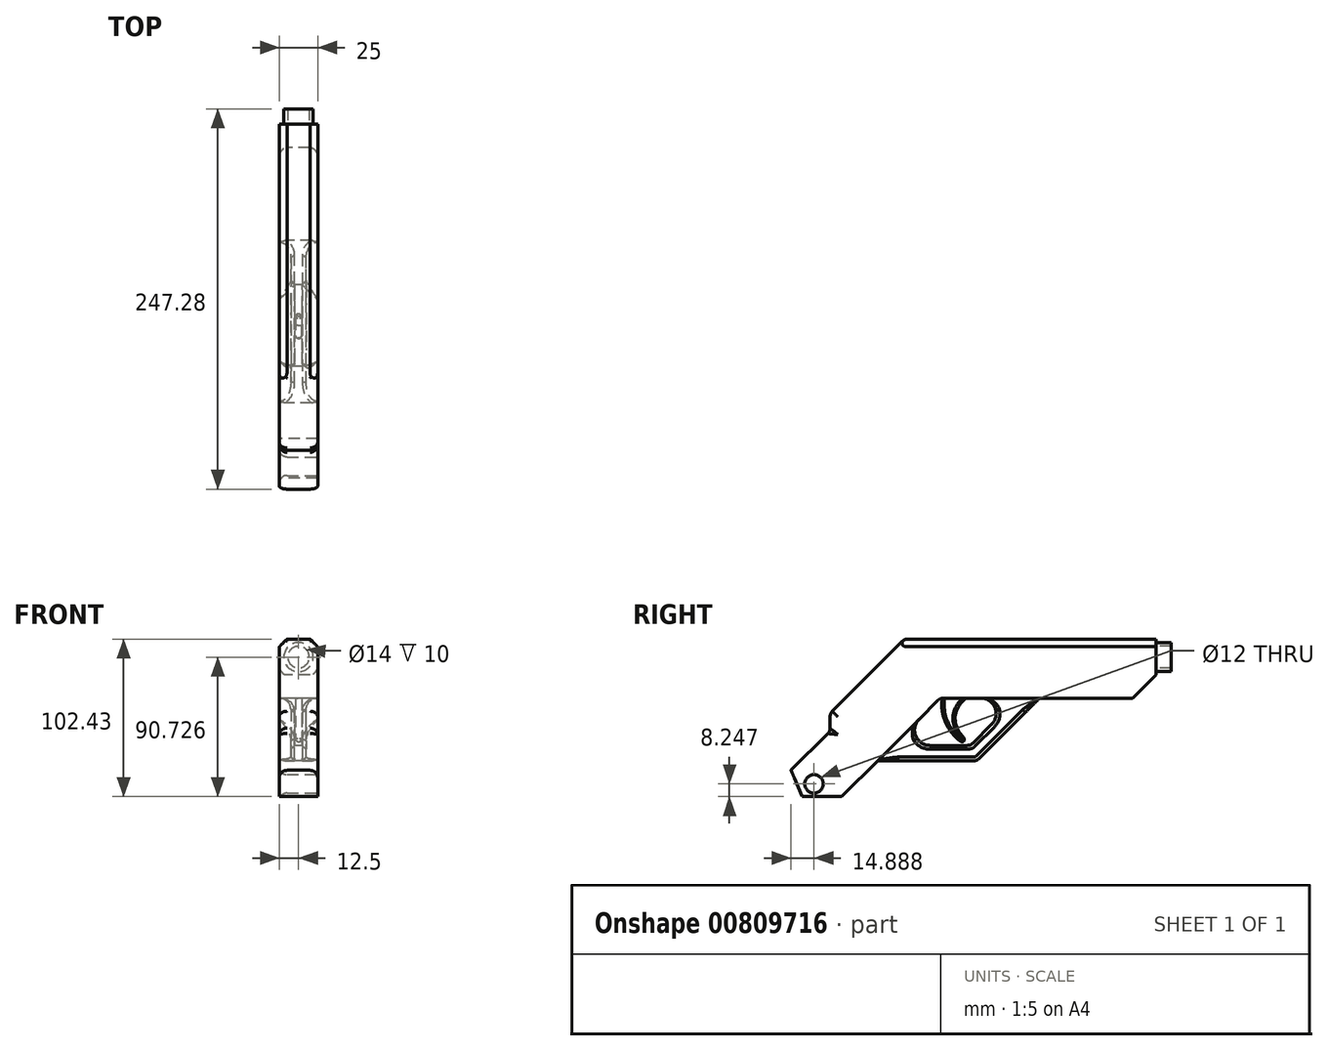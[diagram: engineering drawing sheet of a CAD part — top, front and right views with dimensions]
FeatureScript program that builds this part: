
annotation { "Feature Type Name" : "Feature", "Feature Type Description" : "" }
export const myFeature = defineFeature(function(context is Context, id is Id, definition is map)
    precondition{}
    {
        {
            var Q0;
            Q0=qCreatedBy(makeId("Right.planeOp"),FACE);
            var sketch = newSketch(context, id + "F0", { "sketchPlane" : qUnion([Q0])});
            skLineSegment(sketch, "E0", {"start": v(-96.29, 0) * mm, "end": v(-96.29, 15) * mm});
            skLineSegment(sketch, "E1", {"start": v(-96.29, 15) * mm, "end": v(75.64, 15) * mm});
            skLineSegment(sketch, "E2", {"start": v(75.64, 15) * mm, "end": v(75.64, 0) * mm});
            skLineSegment(sketch, "E3", {"start": v(75.64, 0) * mm, "end": v(60.55, -15) * mm});
            skLineSegment(sketch, "E4", {"start": v(60.55, -15) * mm, "end": v(0, -15) * mm});
            skLineSegment(sketch, "E5", {"start": v(0, -15) * mm, "end": v(-10, -25) * mm});
            skLineSegment(sketch, "E6", {"start": v(-10, -25) * mm, "end": v(-96.29, -25) * mm});
            skLineSegment(sketch, "E7", {"start": v(-96.29, -25) * mm, "end": v(-96.29, 0) * mm});
            skLineSegment(sketch, "E8", {"start": v(-96.29, 15) * mm, "end": v(-136.29, -25) * mm});
            skLineSegment(sketch, "E9", {"start": v(-136.29, -25) * mm, "end": v(-136.29, -36.6) * mm});
            skLineSegment(sketch, "E10", {"start": v(-136.29, -36.6) * mm, "end": v(-178.71, -79.02) * mm});
            skLineSegment(sketch, "E11", {"start": v(-178.71, -79.02) * mm, "end": v(-128.71, -79.02) * mm});
            skLineSegment(sketch, "E12", {"start": v(-128.71, -79.02) * mm, "end": v(-74.7, -25) * mm});
            skLineSegment(sketch, "E13", {"start": v(-10, -25) * mm, "end": v(-40.76, -55.76) * mm});
            skLineSegment(sketch, "E14", {"start": v(-40.76, -55.76) * mm, "end": v(-105.46, -55.76) * mm});
            skLineSegment(sketch, "E15", {"start": v(-24.14, -25) * mm, "end": v(-44.9, -45.76) * mm});
            skLineSegment(sketch, "E16", {"start": v(-44.9, -45.76) * mm, "end": v(-95.46, -45.76) * mm});
            skLineSegment(sketch, "E17", {"start": v(-96.29, 15) * mm, "end": v(-87.88, 23.41) * mm});
            skLineSegment(sketch, "E18", {"start": v(-87.88, 23.41) * mm, "end": v(75.64, 23.41) * mm});
            skLineSegment(sketch, "E19", {"start": v(75.64, 23.41) * mm, "end": v(75.64, 15) * mm});
            skLineSegment(sketch, "E20", {"start": v(-74.7, -25) * mm, "end": v(-64.7, -15) * mm});
            skLineSegment(sketch, "E21", {"start": v(-64.7, -15) * mm, "end": v(0, -15) * mm});
            skLineSegment(sketch, "E22", {"start": v(-24.14, -25) * mm, "end": v(-14.14, -15) * mm});
            skSolve(sketch);
        }
        {
            var Q0;
            Q0=makeQuery(id+"F0.imprint","IMPRINT",FACE,{"disambiguationData":[TD([[makeQuery(id+"F0.imprint","IMPRINT",EDGE,{"derivedFrom":sQuery(id+"F0.wireOp",EDGE,"E0")}),1.0]])]});
            var Q1;
            Q1=makeQuery(id+"F0.imprint","IMPRINT",FACE,{"disambiguationData":[TD([[makeQuery(id+"F0.imprint","IMPRINT",EDGE,{"derivedFrom":sQuery(id+"F0.wireOp",EDGE,"E0")}),-1.0]])]});
            var Q2;
            {var subQ1=sQuery(id+"F0.wireOp",EDGE,"E13");Q2=makeQuery(id+"F0.imprint","IMPRINT",FACE,{"disambiguationData":[TD([[makeQuery(id+"F0.imprint","IMPRINT",EDGE,{"derivedFrom":subQ1}),-1.0]])]});}
            var Q3;
            Q3=makeQuery(id+"F0.imprint","IMPRINT",FACE,{"disambiguationData":[TD([[makeQuery(id+"F0.imprint","IMPRINT",EDGE,{"derivedFrom":sQuery(id+"F0.wireOp",EDGE,"E1")}),1.0]])]});
            var Q4;
            {var subQ0=sQuery(id+"F0.wireOp",EDGE,"E5");Q4=makeQuery(id+"F0.imprint","IMPRINT",FACE,{"disambiguationData":[TD([[makeQuery(id+"F0.imprint","IMPRINT",EDGE,{"derivedFrom":subQ0}),-1.0]])]});}
            extrude(context, id + "F1", {"entities" : qUnion([Q0, Q1, Q2, Q3, Q4]), "depth" : 12.5 * mm});
        }
        {
            var Q0;
            Q0=makeQuery(id+"F1.opExtrude","CAP_EDGE",EDGE,{"disambiguationData":[OSD([sQuery(id+"F0.wireOp",EDGE,"E18")])],"isStart":false});
            chamfer(context, id + "F2", {"entities" : qUnion([Q0]), "width" : 5 * mm, "tangentPropagation" : true});
        }
        {
            var Q0;
            {var subQ0=makeQuery(id+"F1.opExtrude","SWEPT_EDGE",EDGE,{"disambiguationData":[OSD([sQuery(id+"F0.wireOp",EDGE,"E10"),sQuery(id+"F0.wireOp",EDGE,"E11")])]});Q0=makeQuery(id+"F9.boolean.opBoolean","MERGE",EDGE,{"derivedFrom":[subQ0,makeQuery(id+"F9.opPattern","COPY",EDGE,{"derivedFrom":subQ0,"instanceName":"1"})]});}
            chamfer(context, id + "F3", {"entities" : qUnion([Q0]), "width" : 10 * mm, "tangentPropagation" : true});
        }
        {
            var Q0;
            {var subQ0=makeQuery(id+"F1.opExtrude","SWEPT_EDGE",EDGE,{"disambiguationData":[OSD([sQuery(id+"F0.wireOp",EDGE,"E12"),sQuery(id+"F0.wireOp",EDGE,"E16")])]});Q0=makeQuery(id+"F9.boolean.opBoolean","MERGE",EDGE,{"derivedFrom":[subQ0,makeQuery(id+"F9.opPattern","COPY",EDGE,{"derivedFrom":subQ0,"instanceName":"1"})]});}
            var Q1;
            {var subQ0=makeQuery(id+"F1.opExtrude","SWEPT_EDGE",EDGE,{"disambiguationData":[OSD([sQuery(id+"F0.wireOp",EDGE,"E21"),sQuery(id+"F0.wireOp",EDGE,"E22")])]});Q1=makeQuery(id+"F9.boolean.opBoolean","MERGE",EDGE,{"derivedFrom":[subQ0,makeQuery(id+"F9.opPattern","COPY",EDGE,{"derivedFrom":subQ0,"instanceName":"1"})]});}
            fillet(context, id + "F4", {"entities" : qUnion([Q0, Q1]), "radius" : 10 * mm, "tangentPropagation" : true, "allowEdgeOverflow" : false});
        }
        {
            var Q0;
            Q0=makeQuery(id+"F1.opExtrude","CAP_FACE",FACE,{"disambiguationData":[OSD([sQuery(id+"F0.wireOp",EDGE,"E2"),sQuery(id+"F0.wireOp",EDGE,"E3"),sQuery(id+"F0.wireOp",EDGE,"E4"),sQuery(id+"F0.wireOp",EDGE,"E5"),sQuery(id+"F0.wireOp",EDGE,"E8"),sQuery(id+"F0.wireOp",EDGE,"E9"),sQuery(id+"F0.wireOp",EDGE,"E10"),sQuery(id+"F0.wireOp",EDGE,"E11"),sQuery(id+"F0.wireOp",EDGE,"E12"),sQuery(id+"F0.wireOp",EDGE,"E13"),sQuery(id+"F0.wireOp",EDGE,"E14"),sQuery(id+"F0.wireOp",EDGE,"E15"),sQuery(id+"F0.wireOp",EDGE,"E16"),sQuery(id+"F0.wireOp",EDGE,"E17"),sQuery(id+"F0.wireOp",EDGE,"E18"),sQuery(id+"F0.wireOp",EDGE,"E19"),sQuery(id+"F0.wireOp",EDGE,"E20"),sQuery(id+"F0.wireOp",EDGE,"E21"),sQuery(id+"F0.wireOp",EDGE,"E22")])],"isStart":false});
            var sketch = newSketch(context, id + "F5", { "sketchPlane" : qUnion([Q0])});
            skLineSegment(sketch, "E23.0", {"start": v(-128.71, -79.02) * mm, "end": v(-105.46, -55.76) * mm});
            skLineSegment(sketch, "E24.0", {"start": v(-40.76, -55.76) * mm, "end": v(-105.46, -55.76) * mm});
            skLineSegment(sketch, "E25.0", {"start": v(0, -15) * mm, "end": v(-40.76, -55.76) * mm});
            skLineSegment(sketch, "E26.0", {"start": v(-78.39, -28.7) * mm, "end": v(-64.7, -15) * mm});
            skLineSegment(sketch, "E27", {"start": v(-105.46, -55.76) * mm, "end": v(-78.39, -28.7) * mm});
            skLineSegment(sketch, "E28", {"start": v(-64.7, -15) * mm, "end": v(0, -15) * mm});
            skSolve(sketch);
        }
        {
            var Q0;
            Q0=makeQuery(id+"F5.imprint","IMPRINT",FACE,{"disambiguationData":[TD([[makeQuery(id+"F5.imprint","IMPRINT",EDGE,{"derivedFrom":sQuery(id+"F5.wireOp",EDGE,"E24.0")}),-1.0]])]});
            extrude(context, id + "F6", {"entities" : qUnion([Q0]), "operationType" : NewBodyOperationType.REMOVE, "oppositeDirection" : true, "depth" : 7.5 * mm});
        }
        {
            var Q0;
            {var subQ0=sQuery(id+"F0.wireOp",EDGE,"E12");Q0=makeQuery(id+"F6.boolean.opBoolean","MERGE",EDGE,{"derivedFrom":[makeQuery(id+"F1.opExtrude","CAP_EDGE",EDGE,{"disambiguationData":[OSD([subQ0])],"isStart":false}),makeQuery(id+"F1.opExtrude","CAP_EDGE",EDGE,{"disambiguationData":[OSD([subQ0,sQuery(id+"F0.wireOp",EDGE,"E20")])],"isStart":false}),makeQuery(id+"F6.opExtrude","CAP_EDGE",EDGE,{"disambiguationData":[OSD([sQuery(id+"F5.wireOp",EDGE,"E27")])],"isStart":true})]});}
            var Q1;
            Q1=makeQuery(id+"F1.opExtrude","CAP_EDGE",EDGE,{"disambiguationData":[OSD([sQuery(id+"F0.wireOp",EDGE,"E10")])],"isStart":false});
            var Q2;
            Q2=makeQuery(id+"F1.opExtrude","CAP_EDGE",EDGE,{"disambiguationData":[OSD([sQuery(id+"F0.wireOp",EDGE,"E9")])],"isStart":false});
            var Q3;
            Q3=makeQuery(id+"F1.opExtrude","CAP_EDGE",EDGE,{"disambiguationData":[OSD([sQuery(id+"F0.wireOp",EDGE,"E8"),sQuery(id+"F0.wireOp",EDGE,"E17")])],"isStart":false});
            fillet(context, id + "F7", {"entities" : qUnion([Q0, Q1, Q2, Q3]), "radius" : 5 * mm, "tangentPropagation" : true, "allowEdgeOverflow" : false});
        }
        {
            var Q0;
            Q0=makeQuery(id+"F1.opExtrude","SWEPT_EDGE",EDGE,{"disambiguationData":[OSD([sQuery(id+"F0.wireOp",EDGE,"E13"),sQuery(id+"F0.wireOp",EDGE,"E14")])]});
            var Q1;
            Q1=makeQuery(id+"F1.opExtrude","SWEPT_EDGE",EDGE,{"disambiguationData":[OSD([sQuery(id+"F0.wireOp",EDGE,"E15"),sQuery(id+"F0.wireOp",EDGE,"E16")])]});
            var Q2;
            Q2=makeQuery(id+"F1.opExtrude","SWEPT_EDGE",EDGE,{"disambiguationData":[OSD([sQuery(id+"F0.wireOp",EDGE,"E20"),sQuery(id+"F0.wireOp",EDGE,"E21")])]});
            fillet(context, id + "F8", {"entities" : qUnion([Q0, Q1, Q2]), "radius" : 5 * mm, "tangentPropagation" : true, "allowEdgeOverflow" : false});
        }
        {
            var Q0;
            Q0=makeQuery(id+"F1.opExtrude","SWEPT_BODY",BODY,{"disambiguationData":[OSD([sQuery(id+"F0.wireOp",EDGE,"E1"),sQuery(id+"F0.wireOp",EDGE,"E2"),sQuery(id+"F0.wireOp",EDGE,"E3"),sQuery(id+"F0.wireOp",EDGE,"E4"),sQuery(id+"F0.wireOp",EDGE,"E5"),sQuery(id+"F0.wireOp",EDGE,"E6"),sQuery(id+"F0.wireOp",EDGE,"E8"),sQuery(id+"F0.wireOp",EDGE,"E9"),sQuery(id+"F0.wireOp",EDGE,"E10"),sQuery(id+"F0.wireOp",EDGE,"E11"),sQuery(id+"F0.wireOp",EDGE,"E12"),sQuery(id+"F0.wireOp",EDGE,"E13"),sQuery(id+"F0.wireOp",EDGE,"E14"),sQuery(id+"F0.wireOp",EDGE,"E15"),sQuery(id+"F0.wireOp",EDGE,"E16")])]});
            var Q1;
            Q1=qCreatedBy(makeId("Right.planeOp"),FACE);
            mirror(context, id + "F9", {"operationType" : NewBodyOperationType.ADD, "entities" : qUnion([Q0]), "mirrorPlane" : qUnion([Q1])});
        }
        {
            var Q0;
            Q0=makeQuery(id+"F6.boolean.opBoolean","COPY",EDGE,{"derivedFrom":makeQuery(id+"F6.opExtrude","CAP_EDGE",EDGE,{"disambiguationData":[OSD([sQuery(id+"F5.wireOp",EDGE,"E27")])],"isStart":false})});
            var Q1;
            Q1=makeQuery(id+"F9.opPattern","COPY",EDGE,{"derivedFrom":makeQuery(id+"F6.boolean.opBoolean","COPY",EDGE,{"derivedFrom":makeQuery(id+"F6.opExtrude","CAP_EDGE",EDGE,{"disambiguationData":[OSD([sQuery(id+"F5.wireOp",EDGE,"E27")])],"isStart":false})}),"instanceName":"1"});
            var Q2;
            Q2=makeQuery(id+"F9.opPattern","COPY",EDGE,{"derivedFrom":makeQuery(id+"F6.boolean.opBoolean","COPY",EDGE,{"derivedFrom":makeQuery(id+"F6.opExtrude","CAP_EDGE",EDGE,{"disambiguationData":[OSD([sQuery(id+"F5.wireOp",EDGE,"E28")])],"isStart":false})}),"instanceName":"1"});
            var Q3;
            Q3=makeQuery(id+"F6.boolean.opBoolean","COPY",EDGE,{"derivedFrom":makeQuery(id+"F6.opExtrude","CAP_EDGE",EDGE,{"disambiguationData":[OSD([sQuery(id+"F5.wireOp",EDGE,"E28")])],"isStart":false})});
            fillet(context, id + "F10", {"entities" : qUnion([Q0, Q1, Q2, Q3]), "radius" : 7.5 * mm, "tangentPropagation" : true, "allowEdgeOverflow" : false});
        }
        {
            var Q0;
            Q0=makeQuery(id+"F6.boolean.opBoolean","COPY",FACE,{"derivedFrom":makeQuery(id+"F6.opExtrude","CAP_FACE",FACE,{"disambiguationData":[OSD([sQuery(id+"F0.wireOp",EDGE,"E2"),sQuery(id+"F0.wireOp",EDGE,"E3"),sQuery(id+"F0.wireOp",EDGE,"E4"),sQuery(id+"F0.wireOp",EDGE,"E5"),sQuery(id+"F0.wireOp",EDGE,"E8"),sQuery(id+"F0.wireOp",EDGE,"E9"),sQuery(id+"F0.wireOp",EDGE,"E10"),sQuery(id+"F0.wireOp",EDGE,"E11"),sQuery(id+"F0.wireOp",EDGE,"E12"),sQuery(id+"F0.wireOp",EDGE,"E13"),sQuery(id+"F0.wireOp",EDGE,"E14"),sQuery(id+"F0.wireOp",EDGE,"E15"),sQuery(id+"F0.wireOp",EDGE,"E16"),sQuery(id+"F0.wireOp",EDGE,"E17"),sQuery(id+"F0.wireOp",EDGE,"E18"),sQuery(id+"F0.wireOp",EDGE,"E19"),sQuery(id+"F0.wireOp",EDGE,"E20"),sQuery(id+"F0.wireOp",EDGE,"E21"),sQuery(id+"F0.wireOp",EDGE,"E22"),sQuery(id+"F5.wireOp",EDGE,"E24.0"),sQuery(id+"F5.wireOp",EDGE,"E25.0"),sQuery(id+"F5.wireOp",EDGE,"E27"),sQuery(id+"F5.wireOp",EDGE,"E28")])],"isStart":false})});
            var Q1;
            Q1=makeQuery(id+"F9.opPattern","COPY",FACE,{"derivedFrom":makeQuery(id+"F6.boolean.opBoolean","COPY",FACE,{"derivedFrom":makeQuery(id+"F6.opExtrude","CAP_FACE",FACE,{"disambiguationData":[OSD([sQuery(id+"F0.wireOp",EDGE,"E2"),sQuery(id+"F0.wireOp",EDGE,"E3"),sQuery(id+"F0.wireOp",EDGE,"E4"),sQuery(id+"F0.wireOp",EDGE,"E5"),sQuery(id+"F0.wireOp",EDGE,"E8"),sQuery(id+"F0.wireOp",EDGE,"E9"),sQuery(id+"F0.wireOp",EDGE,"E10"),sQuery(id+"F0.wireOp",EDGE,"E11"),sQuery(id+"F0.wireOp",EDGE,"E12"),sQuery(id+"F0.wireOp",EDGE,"E13"),sQuery(id+"F0.wireOp",EDGE,"E14"),sQuery(id+"F0.wireOp",EDGE,"E15"),sQuery(id+"F0.wireOp",EDGE,"E16"),sQuery(id+"F0.wireOp",EDGE,"E17"),sQuery(id+"F0.wireOp",EDGE,"E18"),sQuery(id+"F0.wireOp",EDGE,"E19"),sQuery(id+"F0.wireOp",EDGE,"E20"),sQuery(id+"F0.wireOp",EDGE,"E21"),sQuery(id+"F0.wireOp",EDGE,"E22"),sQuery(id+"F5.wireOp",EDGE,"E24.0"),sQuery(id+"F5.wireOp",EDGE,"E25.0"),sQuery(id+"F5.wireOp",EDGE,"E27"),sQuery(id+"F5.wireOp",EDGE,"E28")])],"isStart":false})}),"instanceName":"1"});
            chamfer(context, id + "F11", {"entities" : qUnion([Q0, Q1]), "width" : 2.5 * mm, "tangentPropagation" : true});
        }
        {
            var Q0;
            Q0=qCreatedBy(makeId("Right.planeOp"),FACE);
            var sketch = newSketch(context, id + "F12", { "sketchPlane" : qUnion([Q0])});
            skFitSpline(sketch, "E29", {"points": [v(-62.96, -12.46) * mm, v(-63.47, -22.09) * mm, v(-59.18, -34.62) * mm, v(-51.22, -43.05) * mm, v(-49.2, -42.9) * mm, v(-49.2, -41.2) * mm, v(-52.56, -36.49) * mm, v(-54.7, -25.52) * mm, v(-49.2, -16.13) * mm, v(-46.48, -14.3) * mm], "startDerivative": vector(-9.56, -71.32) * mm, "endDerivative": vector(32.46, 16.46) * mm});
            skLineSegment(sketch, "E30", {"start": v(-62.96, -12.46) * mm, "end": v(-61.97, -8.35) * mm});
            skLineSegment(sketch, "E31", {"start": v(-61.97, -8.35) * mm, "end": v(-46.48, -8.35) * mm});
            skLineSegment(sketch, "E32", {"start": v(-46.48, -8.35) * mm, "end": v(-46.48, -14.3) * mm});
            skSolve(sketch);
        }
        {
            var Q0;
            Q0=makeQuery(id+"F12.imprint","IMPRINT",FACE,{"disambiguationData":[TD([[makeQuery(id+"F12.imprint","IMPRINT",EDGE,{"derivedFrom":sQuery(id+"F12.wireOp",EDGE,"E29")}),1.0]])]});
            extrude(context, id + "F13", {"entities" : qUnion([Q0]), "operationType" : NewBodyOperationType.ADD, "endBound" : BoundingType.SYMMETRIC, "depth" : 4 * mm, "offsetDistance" : 25 * mm});
        }
        {
            var Q0;
            Q0=makeQuery(id+"F13.opExtrude","CAP_EDGE",EDGE,{"disambiguationData":[OSD([sQuery(id+"F12.wireOp",EDGE,"E29")])],"isStart":true});
            var Q1;
            Q1=makeQuery(id+"F13.opExtrude","CAP_EDGE",EDGE,{"disambiguationData":[OSD([sQuery(id+"F12.wireOp",EDGE,"E29")])],"isStart":false});
            fillet(context, id + "F14", {"entities" : qUnion([Q0, Q1]), "radius" : 1.5 * mm, "tangentPropagation" : true, "allowEdgeOverflow" : false});
        }
        {
            var Q0;
            {var subQ0=makeQuery(id+"F1.opExtrude","SWEPT_FACE",FACE,{"disambiguationData":[OSD([sQuery(id+"F0.wireOp",EDGE,"E2"),sQuery(id+"F0.wireOp",EDGE,"E19")])]});Q0=makeQuery(id+"F9.boolean.opBoolean","MERGE",FACE,{"derivedFrom":[subQ0,makeQuery(id+"F9.opPattern","COPY",FACE,{"derivedFrom":subQ0,"instanceName":"1"})]});}
            var sketch = newSketch(context, id + "F15", { "sketchPlane" : qUnion([Q0])});
            skLineSegment(sketch, "E33", {"start": v(0, 23.41) * mm, "end": v(0, 0) * mm});
            skCircle(sketch, "E34", {"center": v(0, 11.7) * mm, "radius": 9.5 * mm});
            skCircle(sketch, "E35.0", {"center": v(0, 11.7) * mm, "radius": 7 * mm});
            skSolve(sketch);
        }
        {
            var Q0;
            {var subQ0=sQuery(id+"F15.wireOp",EDGE,"E34");var subQ1=sQuery(id+"F15.wireOp",EDGE,"E33");var subQ2=makeQuery(id+"F15.imprint","INTERSECT",VERTEX,{"disambiguationData":[OD(0.0)],"derivedFrom":[subQ1,subQ0]});Q0=makeQuery(id+"F15.imprint","IMPRINT",FACE,{"disambiguationData":[TD([[makeQuery(id+"F15.imprint","IMPRINT",EDGE,{"disambiguationData":[TD([[subQ2,-1.0]])],"derivedFrom":subQ1}),-1.0]])]});}
            var Q1;
            {var subQ0=sQuery(id+"F15.wireOp",EDGE,"E34");var subQ1=sQuery(id+"F15.wireOp",EDGE,"E33");var subQ2=makeQuery(id+"F15.imprint","INTERSECT",VERTEX,{"disambiguationData":[OD(0.0)],"derivedFrom":[subQ1,subQ0]});Q1=makeQuery(id+"F15.imprint","IMPRINT",FACE,{"disambiguationData":[TD([[makeQuery(id+"F15.imprint","IMPRINT",EDGE,{"disambiguationData":[TD([[subQ2,-1.0]])],"derivedFrom":subQ1}),1.0]])]});}
            extrude(context, id + "F16", {"entities" : qUnion([Q0, Q1]), "operationType" : NewBodyOperationType.ADD, "depth" : 10 * mm, "offsetDistance" : 25 * mm});
        }
        {
            var Q0;
            Q0=makeQuery(id+"F9.opPattern","COPY",EDGE,{"derivedFrom":makeQuery(id+"F1.opExtrude","CAP_EDGE",EDGE,{"disambiguationData":[OSD([sQuery(id+"F0.wireOp",EDGE,"E3")])],"isStart":false}),"instanceName":"1"});
            var Q1;
            Q1=makeQuery(id+"F1.opExtrude","CAP_EDGE",EDGE,{"disambiguationData":[OSD([sQuery(id+"F0.wireOp",EDGE,"E3")])],"isStart":false});
            var Q2;
            {var subQ0=makeQuery(id+"F1.opExtrude","SWEPT_EDGE",EDGE,{"disambiguationData":[OSD([sQuery(id+"F0.wireOp",EDGE,"E17"),sQuery(id+"F0.wireOp",EDGE,"E18")])]});Q2=makeQuery(id+"F9.boolean.opBoolean","MERGE",EDGE,{"derivedFrom":[subQ0,makeQuery(id+"F9.opPattern","COPY",EDGE,{"derivedFrom":subQ0,"instanceName":"1"})]});}
            var Q3;
            {var subQ0=makeQuery(id+"F1.opExtrude","SWEPT_EDGE",EDGE,{"disambiguationData":[OSD([sQuery(id+"F0.wireOp",EDGE,"E8"),sQuery(id+"F0.wireOp",EDGE,"E9")])]});Q3=makeQuery(id+"F9.boolean.opBoolean","MERGE",EDGE,{"derivedFrom":[subQ0,makeQuery(id+"F9.opPattern","COPY",EDGE,{"derivedFrom":subQ0,"instanceName":"1"})]});}
            var Q4;
            {var subQ0=makeQuery(id+"F1.opExtrude","SWEPT_EDGE",EDGE,{"disambiguationData":[OSD([sQuery(id+"F0.wireOp",EDGE,"E9"),sQuery(id+"F0.wireOp",EDGE,"E10")])]});Q4=makeQuery(id+"F9.boolean.opBoolean","MERGE",EDGE,{"derivedFrom":[subQ0,makeQuery(id+"F9.opPattern","COPY",EDGE,{"derivedFrom":subQ0,"instanceName":"1"})]});}
            fillet(context, id + "F17", {"entities" : qUnion([Q0, Q1, Q2, Q3, Q4]), "radius" : 5 * mm, "tangentPropagation" : true, "allowEdgeOverflow" : false});
        }
        {
            var Q0;
            Q0=makeQuery(id+"F1.opExtrude","CAP_FACE",FACE,{"disambiguationData":[OSD([sQuery(id+"F0.wireOp",EDGE,"E2"),sQuery(id+"F0.wireOp",EDGE,"E3"),sQuery(id+"F0.wireOp",EDGE,"E4"),sQuery(id+"F0.wireOp",EDGE,"E5"),sQuery(id+"F0.wireOp",EDGE,"E8"),sQuery(id+"F0.wireOp",EDGE,"E9"),sQuery(id+"F0.wireOp",EDGE,"E10"),sQuery(id+"F0.wireOp",EDGE,"E11"),sQuery(id+"F0.wireOp",EDGE,"E12"),sQuery(id+"F0.wireOp",EDGE,"E13"),sQuery(id+"F0.wireOp",EDGE,"E14"),sQuery(id+"F0.wireOp",EDGE,"E15"),sQuery(id+"F0.wireOp",EDGE,"E16"),sQuery(id+"F0.wireOp",EDGE,"E17"),sQuery(id+"F0.wireOp",EDGE,"E18"),sQuery(id+"F0.wireOp",EDGE,"E19"),sQuery(id+"F0.wireOp",EDGE,"E20"),sQuery(id+"F0.wireOp",EDGE,"E21"),sQuery(id+"F0.wireOp",EDGE,"E22")])],"isStart":false});
            var sketch = newSketch(context, id + "F18", { "sketchPlane" : qUnion([Q0])});
            skCircle(sketch, "E36", {"center": v(-146.75, -70.77) * mm, "radius": 6 * mm});
            skSolve(sketch);
        }
        {
            var Q0;
            Q0 = qSketchRegion(id + "F18", true);
            extrude(context, id + "F19", {"entities" : qUnion([Q0]), "operationType" : NewBodyOperationType.REMOVE, "oppositeDirection" : true, "depth" : 31.8 * mm, "offsetDistance" : 25 * mm});
        }
        {
            var Q0;
            Q0=makeQuery(id+"F19.boolean.opBoolean","COPY",EDGE,{"derivedFrom":makeQuery(id+"F19.opExtrude","CAP_EDGE",EDGE,{"disambiguationData":[OSD([sQuery(id+"F18.wireOp",EDGE,"E36")])],"isStart":true})});
            var Q1;
            Q1=makeQuery(id+"F19.boolean.opBoolean","INTERSECT",EDGE,{"derivedFrom":[makeQuery(id+"F9.opPattern","COPY",FACE,{"derivedFrom":makeQuery(id+"F1.opExtrude","CAP_FACE",FACE,{"disambiguationData":[OSD([sQuery(id+"F0.wireOp",EDGE,"E2"),sQuery(id+"F0.wireOp",EDGE,"E3"),sQuery(id+"F0.wireOp",EDGE,"E4"),sQuery(id+"F0.wireOp",EDGE,"E5"),sQuery(id+"F0.wireOp",EDGE,"E8"),sQuery(id+"F0.wireOp",EDGE,"E9"),sQuery(id+"F0.wireOp",EDGE,"E10"),sQuery(id+"F0.wireOp",EDGE,"E11"),sQuery(id+"F0.wireOp",EDGE,"E12"),sQuery(id+"F0.wireOp",EDGE,"E13"),sQuery(id+"F0.wireOp",EDGE,"E14"),sQuery(id+"F0.wireOp",EDGE,"E15"),sQuery(id+"F0.wireOp",EDGE,"E16"),sQuery(id+"F0.wireOp",EDGE,"E17"),sQuery(id+"F0.wireOp",EDGE,"E18"),sQuery(id+"F0.wireOp",EDGE,"E19"),sQuery(id+"F0.wireOp",EDGE,"E20"),sQuery(id+"F0.wireOp",EDGE,"E21"),sQuery(id+"F0.wireOp",EDGE,"E22")])],"isStart":false}),"instanceName":"1"}),makeQuery(id+"F19.opExtrude","SWEPT_FACE",FACE,{"disambiguationData":[OSD([sQuery(id+"F18.wireOp",EDGE,"E36")])]})]});
            fillet(context, id + "F20", {"entities" : qUnion([Q0, Q1]), "radius" : 5 * mm, "tangentPropagation" : true, "allowEdgeOverflow" : false});
        }
    });
